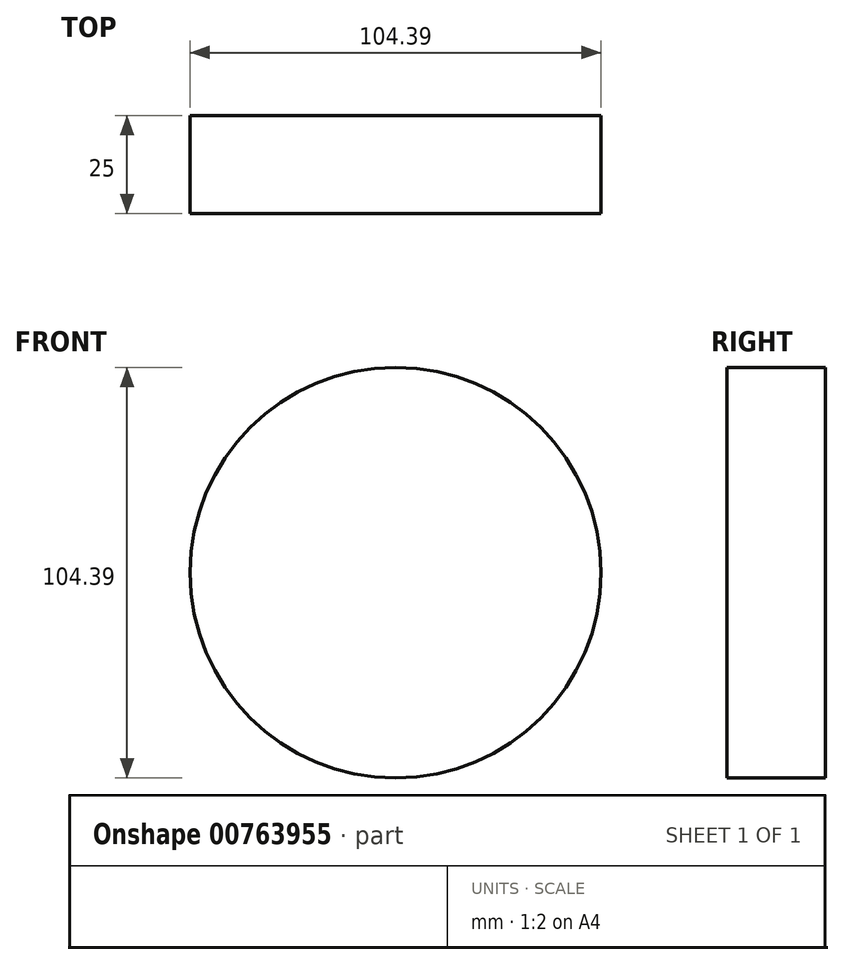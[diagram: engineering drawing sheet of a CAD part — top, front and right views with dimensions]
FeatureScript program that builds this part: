
annotation { "Feature Type Name" : "Feature", "Feature Type Description" : "" }
export const myFeature = defineFeature(function(context is Context, id is Id, definition is map)
    precondition{}
    {
        {
            var Q0;
            Q0=qCreatedBy(makeId("Front.planeOp"),FACE);
            var sketch = newSketch(context, id + "F0", { "sketchPlane" : qUnion([Q0])});
            skCircle(sketch, "E0", {"center": v(-45.92, 51.82) * mm, "radius": 52.2 * mm});
            skSolve(sketch);
        }
        {
            var Q0;
            Q0 = qSketchRegion(id + "F0", true);
            extrude(context, id + "F1", {"entities" : qUnion([Q0]), "depth" : 25 * mm, "offsetDistance" : 25 * mm});
        }
    });
